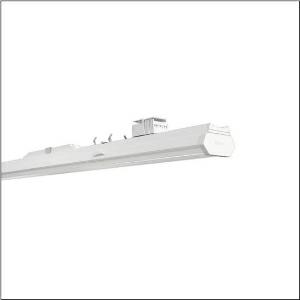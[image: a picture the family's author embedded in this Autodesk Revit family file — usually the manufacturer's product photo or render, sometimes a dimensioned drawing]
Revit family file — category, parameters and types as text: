
# Revit family: licross_21_protected_mo_52td1bcn485g
name_source: partatom
category: Lighting Fixtures
units: mm (PartAtom-declared; Revit-internal decimal feet)

## family parameters
Cut with Voids When Loaded = No
Host = Face
Light Source = No
Part Type = Normal
Room Calculation Point = No
Round Connector Dimension = Use Diameter
Shared = No

## types (1)
- --- (1 x LED, 8570 lm, 50.4 W, 4000K)
    Apparent Load = 50 VA
    CIE Flux Codes = 54 82 95 97 100
    Color Rendering = 80
    Color Temperature = 4000K
    Default Elevation = 1800 mm
    Description = Licross 21 Protected MO, luminaire insert, of sheet steel, galvanised, coil coated, white, length: 1.500mm, width: 90mm, height: 103mm, LED rated luminous flux: 8.570lm, light colour: 840, SDCM (Standard Deviation of Colour Matching)MacAdam ≤ 3 SDCM (initial), control gear: ON/OFF Multilumen, CLOi, with plug, 3-pole, with phase selection, mains connection: 220..240V, AC, 50/60Hz, start of lifetime: 50W, end of service life: 61W, internal wiring halogen-free, primary optical cover: cover, of PMMA, light emission: direct distribution, primary light characteristic: symmetric, protection rating (complete): IP54, insulation class (complete): insulation class I (protective earthing), certification: CE, ENEC, VDE, UKCA, protection symbol: D if used in an environment with non-conductive dust loads with corresponding accessories, impact resistance: IK06, permissible ambient temperature for indoor applications: -35..+45°C, corresponds to IFS (International Featured Standards) requirements for safety and quality in the food industry, reducing of maximum allowable ambient temperature of 5°C with ceiling mounting, LABS conformity tested according to VDMA 24364:2018-05, The light source and the operating device comply with the requirements of the Ecodesign Regulation (EU) 2019/2020 and are replaceable in accordance with this regulation, packaging unit: 1 piece
    Height = 92 mm
    Lamp = 1 x LED
    Lamp Light Flux = 8570 lm
    Lamp Power = 50.4 W
    Lamp count = 1
    Length = 1500 mm
    Luminous efficacy = 170 lm/W
    Manufacturer = Siteco
    ModVariant = No
    Model = 52TD1BCN485G
    Mounting Place = Ceiling
    Mounting Type = Pendant
    Number of Poles = 1
    OnlyDefault = Yes
    Power Factor = 1
    Product Name = Licross 21 Protected MO
    Product group = luminaire insert | ceiling pendant
    ProductGroupID = 901
    Protection Class = Protection class I
    Protection Degree = IP 54
    RLX_Detail_Level = 1
    RLX_Emergency_Light_Flux = 0 lm
    RLX_Emergency_Type = 0
    RLX_Emergency_Type_DB = No
    RlxData = <blob elided: 22349 chars, md5=f94bacc5>
    Socket = socket
    Standby Power = 0 W
    System Light Flux = 8570 lm
    System Power = 50 W
    Type Comments = factory setting: luminous flux: 100 % | (A | C | E) | 117 mA
    Type Image = l_1256148.jpg
    URL = http://relux.com
    VarID = @adj_111465
    Voltage = 0 V
    Weight = 0.00 kg
    Width = 88 mm

## geometry (parser evidence)
native form markers: Blend x4, Sweep x9
no freeform markers — native parametric forms only
